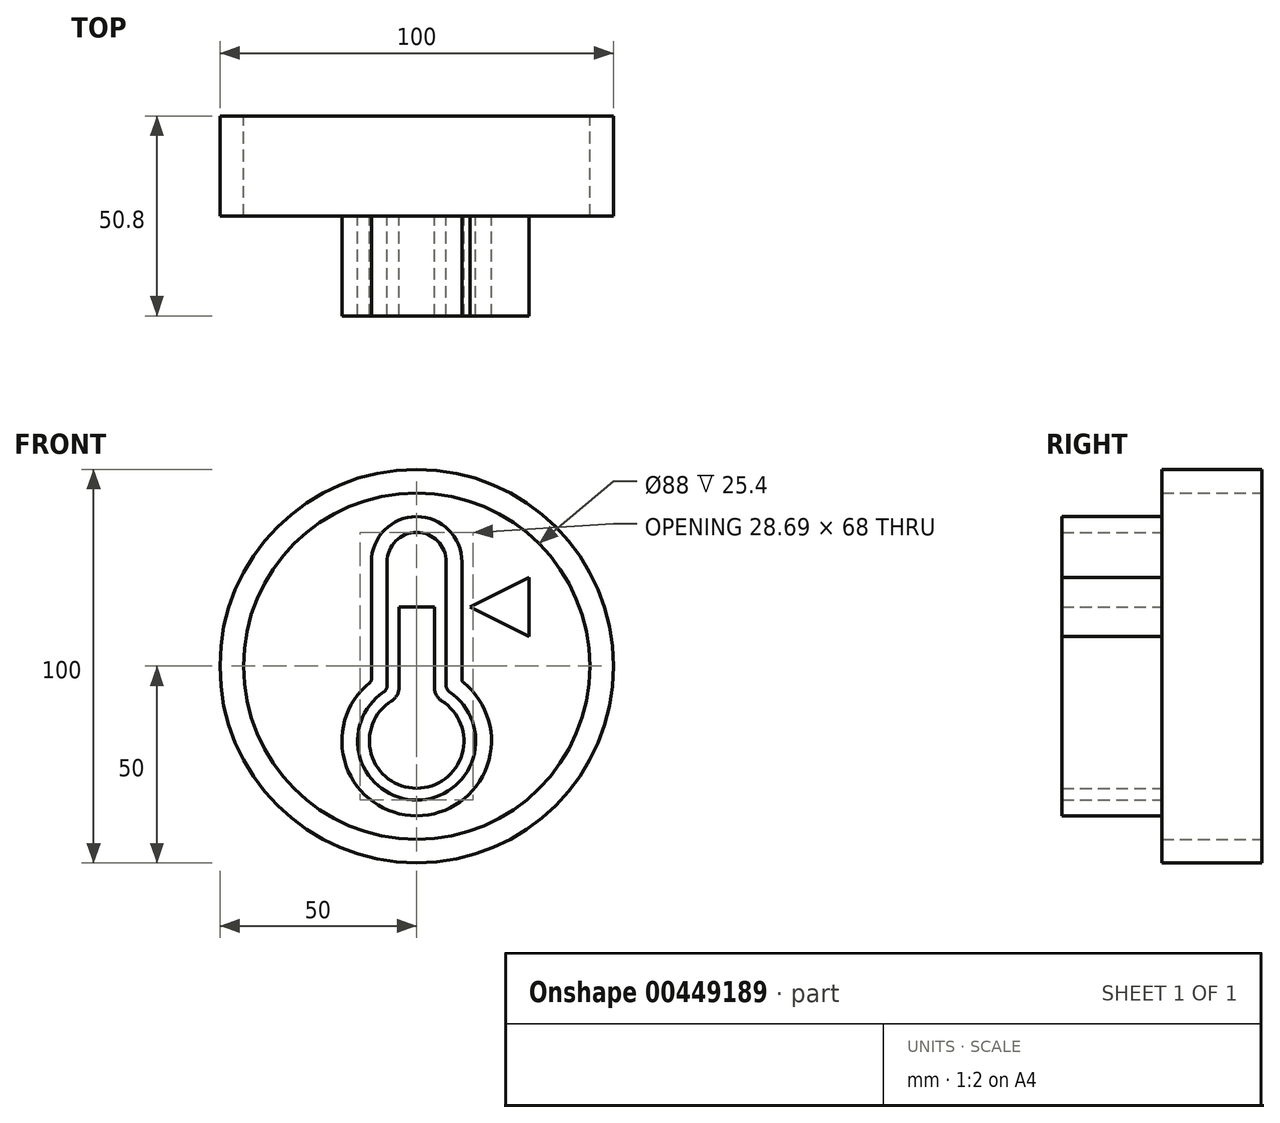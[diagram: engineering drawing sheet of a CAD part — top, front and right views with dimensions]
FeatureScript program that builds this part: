
annotation { "Feature Type Name" : "Feature", "Feature Type Description" : "" }
export const myFeature = defineFeature(function(context is Context, id is Id, definition is map)
    precondition{}
    {
        {
            var Q0;
            Q0=qCreatedBy(makeId("Front.planeOp"),FACE);
            var sketch = newSketch(context, id + "F0", { "sketchPlane" : qUnion([Q0])});
            skCircle(sketch, "E0", {"center": v(0, 0) * mm, "radius": 50 * mm});
            skCircle(sketch, "E1", {"center": v(0, 0) * mm, "radius": 44 * mm});
            skLineSegment(sketch, "E2", {"start": v(0, -40) * mm, "end": v(-28.83, -1.31) * mm});
            skArc(sketch, "E3", {"start": v(0, 8.25) * mm, "mid": v(-21.04, 23.43) * mm, "end": v(-28.83, -1.31) * mm});
            skLineSegment(sketch, "E4", {"start": v(-39.11, 20.16) * mm, "end": v(0, 0) * mm});
            skPoint(sketch, "E5", {"position": v(-30.22, 15.58) * mm});
            skPoint(sketch, "E6", {"position": v(0, -50) * mm});
            skLineSegment(sketch, "E7", {"start": v(-30.22, 15.58) * mm, "end": v(-38.08, 0.33) * mm});
            skLineSegment(sketch, "E8", {"start": v(0, 8.25) * mm, "end": v(0, -40) * mm});
            skLineSegment(sketch, "E9.MirrorCS", {"start": v(0, -40) * mm, "end": v(28.83, -1.31) * mm});
            skArc(sketch, "E10.MirrorCS", {"start": v(0, 8.25) * mm, "mid": v(21.04, 23.43) * mm, "end": v(28.83, -1.31) * mm});
            skArc(sketch, "E11.0", {"start": v(0, 16.5) * mm, "mid": v(25.53, 23.51) * mm, "end": v(30.43, -2.5) * mm});
            skArc(sketch, "E11.1", {"start": v(0, 16.5) * mm, "mid": v(-25.53, 23.51) * mm, "end": v(-30.43, -2.5) * mm});
            skLineSegment(sketch, "E11.2", {"start": v(0, -43.35) * mm, "end": v(-30.43, -2.5) * mm});
            skLineSegment(sketch, "E11.3", {"start": v(0, -43.35) * mm, "end": v(30.43, -2.5) * mm});
            skSolve(sketch);
        }
        {
            var Q0;
            Q0=makeQuery(id+"F0.imprint","IMPRINT",FACE,{"disambiguationData":[TD([[makeQuery(id+"F0.imprint","IMPRINT",EDGE,{"derivedFrom":sQuery(id+"F0.wireOp",EDGE,"E0")}),1.0]])]});
            var Q1;
            {var subQ9=sQuery(id+"F0.wireOp",EDGE,"E2");Q1=makeQuery(id+"F0.imprint","IMPRINT",FACE,{"disambiguationData":[TD([[makeQuery(id+"F0.imprint","IMPRINT",EDGE,{"derivedFrom":subQ9}),1.0]])]});}
            var Q2;
            {var subQ1=sQuery(id+"F0.wireOp",EDGE,"E4");var subQ3=sQuery(id+"F0.wireOp",EDGE,"E11.1");var subQ4=makeQuery(id+"F0.imprint","INTERSECT",VERTEX,{"derivedFrom":[subQ1,subQ3]});Q2=makeQuery(id+"F0.imprint","IMPRINT",FACE,{"disambiguationData":[TD([[makeQuery(id+"F0.imprint","IMPRINT",EDGE,{"disambiguationData":[TD([[subQ4,-1.0]])],"derivedFrom":subQ3}),1.0]])]});}
            extrude(context, id + "F1", {"entities" : qUnion([Q0, Q1, Q2]), "depth" : 25.4 * mm});
        }
        {
            var Q0;
            Q0=makeQuery(id+"F1.opExtrude","SWEPT_EDGE",EDGE,{"disambiguationData":[OSD([sQuery(id+"F0.wireOp",EDGE,"E11.0"),sQuery(id+"F0.wireOp",EDGE,"E11.1")])]});
            fillet(context, id + "F2", {"entities" : qUnion([Q0]), "radius" : 1 * mm, "tangentPropagation" : true, "allowEdgeOverflow" : false});
        }
        {
            var Q0;
            Q0=makeQuery(id+"F1.opExtrude","SWEPT_EDGE",EDGE,{"disambiguationData":[OSD([sQuery(id+"F0.wireOp",EDGE,"E3"),sQuery(id+"F0.wireOp",EDGE,"E8"),sQuery(id+"F0.wireOp",EDGE,"E10.MirrorCS")])]});
            fillet(context, id + "F3", {"entities" : qUnion([Q0]), "radius" : 2 * mm, "tangentPropagation" : true, "allowEdgeOverflow" : false});
        }
        {
            var Q0;
            Q0=makeQuery(id+"F1.opExtrude","SWEPT_EDGE",EDGE,{"disambiguationData":[OSD([sQuery(id+"F0.wireOp",EDGE,"E2"),sQuery(id+"F0.wireOp",EDGE,"E8"),sQuery(id+"F0.wireOp",EDGE,"E9.MirrorCS")])]});
            fillet(context, id + "F4", {"entities" : qUnion([Q0]), "radius" : 1 * mm, "tangentPropagation" : true, "allowEdgeOverflow" : false});
        }
        {
            var Q0;
            Q0=makeQuery(id+"F1.opExtrude","SWEPT_EDGE",EDGE,{"disambiguationData":[OSD([sQuery(id+"F0.wireOp",EDGE,"E11.2"),sQuery(id+"F0.wireOp",EDGE,"E11.3")])]});
            fillet(context, id + "F5", {"entities" : qUnion([Q0]), "radius" : 2 * mm, "tangentPropagation" : true, "allowEdgeOverflow" : false});
        }
        {
            var Q0;
            Q0=makeQuery(id+"F1.opExtrude","SWEPT_BODY",BODY,{"disambiguationData":[OSD([sQuery(id+"F0.wireOp",EDGE,"E2"),sQuery(id+"F0.wireOp",EDGE,"E3"),sQuery(id+"F0.wireOp",EDGE,"E9.MirrorCS"),sQuery(id+"F0.wireOp",EDGE,"E10.MirrorCS"),sQuery(id+"F0.wireOp",EDGE,"E11.0"),sQuery(id+"F0.wireOp",EDGE,"E11.1"),sQuery(id+"F0.wireOp",EDGE,"E11.2"),sQuery(id+"F0.wireOp",EDGE,"E11.3")])]});
            deleteBodies(context, id + "F6", {"entities" : qUnion([Q0])});
        }
        {
            var Q0;
            Q0=makeQuery(id+"F1.opExtrude","CAP_FACE",FACE,{"disambiguationData":[OSD([sQuery(id+"F0.wireOp",EDGE,"E0"),sQuery(id+"F0.wireOp",EDGE,"E1")])],"isStart":false});
            var sketch = newSketch(context, id + "F7", { "sketchPlane" : qUnion([Q0])});
            skArc(sketch, "E12", {"start": v(-7.5, -6) * mm, "mid": v(0, -34) * mm, "end": v(7.5, -6) * mm});
            skPoint(sketch, "E13", {"position": v(0, -34) * mm});
            skArc(sketch, "E14", {"start": v(7.5, 26.5) * mm, "mid": v(0, 34) * mm, "end": v(-7.5, 26.5) * mm});
            skLineSegment(sketch, "E15.left", {"start": v(-7.5, 26.5) * mm, "end": v(-7.5, -6) * mm});
            skLineSegment(sketch, "E15.right", {"start": v(7.5, 26.5) * mm, "end": v(7.5, -6) * mm});
            skPoint(sketch, "E16.orphan", {"position": v(-7.5, -19) * mm});
            skLineSegment(sketch, "E17.0", {"start": v(-11.5, 26.5) * mm, "end": v(-11.5, -3.88) * mm});
            skArc(sketch, "E17.1", {"start": v(11.5, 26.5) * mm, "mid": v(0, 38) * mm, "end": v(-11.5, 26.5) * mm});
            skLineSegment(sketch, "E17.2", {"start": v(11.5, 26.5) * mm, "end": v(11.5, -3.88) * mm});
            skArc(sketch, "E17.3", {"start": v(-11.5, -3.88) * mm, "mid": v(0, -38) * mm, "end": v(11.5, -3.88) * mm});
            skLineSegment(sketch, "E18.0", {"start": v(-4.5, 15) * mm, "end": v(-4.5, -7.88) * mm});
            skArc(sketch, "E18.1", {"start": v(-4.5, -7.88) * mm, "mid": v(0, -31) * mm, "end": v(4.5, -7.88) * mm});
            skLineSegment(sketch, "E18.2", {"start": v(4.5, 15) * mm, "end": v(4.5, -7.88) * mm});
            skLineSegment(sketch, "E19", {"start": v(-4.5, 15) * mm, "end": v(4.5, 15) * mm});
            skLineSegment(sketch, "E20", {"start": v(13.5, 15) * mm, "end": v(28.5, 22.5) * mm});
            skLineSegment(sketch, "E21", {"start": v(28.5, 22.5) * mm, "end": v(28.5, 7.5) * mm});
            skLineSegment(sketch, "E22", {"start": v(28.5, 7.5) * mm, "end": v(13.5, 15) * mm});
            skPoint(sketch, "E23", {"position": v(28.5, 15) * mm});
            skSolve(sketch);
        }
        {
            var Q0;
            Q0 = qSketchRegion(id + "F7", true);
            var Q1;
            Q1=makeQuery(id+"F7.imprint","IMPRINT",FACE,{"disambiguationData":[TD([[makeQuery(id+"F7.imprint","IMPRINT",EDGE,{"derivedFrom":sQuery(id+"F7.wireOp",EDGE,"E18.0")}),1.0]])]});
            extrude(context, id + "F8", {"entities" : qUnion([Q0, Q1]), "depth" : 25.4 * mm});
        }
        {
            var Q0;
            Q0=makeQuery(id+"F8.opExtrude","SWEPT_EDGE",EDGE,{"disambiguationData":[OSD([sQuery(id+"F7.wireOp",EDGE,"E17.2"),sQuery(id+"F7.wireOp",EDGE,"E17.3")])]});
            var Q1;
            Q1=makeQuery(id+"F8.opExtrude","SWEPT_EDGE",EDGE,{"disambiguationData":[OSD([sQuery(id+"F7.wireOp",EDGE,"E17.0"),sQuery(id+"F7.wireOp",EDGE,"E17.3")])]});
            fillet(context, id + "F9", {"entities" : qUnion([Q0, Q1]), "radius" : 1 * mm, "tangentPropagation" : true, "allowEdgeOverflow" : false});
        }
        {
            var Q0;
            Q0=makeQuery(id+"F8.opExtrude","SWEPT_EDGE",EDGE,{"disambiguationData":[OSD([sQuery(id+"F7.wireOp",EDGE,"E12"),sQuery(id+"F7.wireOp",EDGE,"E15.left")])]});
            var Q1;
            Q1=makeQuery(id+"F8.opExtrude","SWEPT_EDGE",EDGE,{"disambiguationData":[OSD([sQuery(id+"F7.wireOp",EDGE,"E12"),sQuery(id+"F7.wireOp",EDGE,"E15.right")])]});
            fillet(context, id + "F10", {"entities" : qUnion([Q0, Q1]), "radius" : 2 * mm, "tangentPropagation" : true, "allowEdgeOverflow" : false});
        }
        {
            var Q0;
            Q0=makeQuery(id+"F8.opExtrude","SWEPT_EDGE",EDGE,{"disambiguationData":[OSD([sQuery(id+"F7.wireOp",EDGE,"E18.0"),sQuery(id+"F7.wireOp",EDGE,"E18.1")])]});
            var Q1;
            Q1=makeQuery(id+"F8.opExtrude","SWEPT_EDGE",EDGE,{"disambiguationData":[OSD([sQuery(id+"F7.wireOp",EDGE,"E18.1"),sQuery(id+"F7.wireOp",EDGE,"E18.2")])]});
            fillet(context, id + "F11", {"entities" : qUnion([Q0, Q1]), "radius" : 4 * mm, "tangentPropagation" : true, "allowEdgeOverflow" : false});
        }
    });
